# Revit family: IS_CeramixBlue_B9494_BIM_DE
name_source: partatom
category: Plumbing Fixtures
revit_build: Autodesk Revit MEP 2015 (Build: 20140606_1530(x64)
units: mm (PartAtom-declared; Revit-internal decimal feet)

## types (1)
- B9494AA - CERAMIX BLUE kitchen mixer one hole single lever hand, low pressure
    Assembly Code = C1030206
    BIMobject category = Taps & Mixers
    BOSUseNativeGeometries = 1
    Brand url = www.idealstandard.com
    Description = B9494AA CERAMIX BLUE kitchen mixer one hole single lever hand, low pressure
    EAN code = https://4015413318730
    Edition number = 1
    FaucetFunction = mixed
    FaucetOperation = leverhandle
    FaucetType = pillar
    FlushRate = 0 m³
    FlushingRate = 0
    IFC Classification = Valve
    IfcExportAs = Valve
    IfcExportType = KITCHEN TAP
    Installation instructions = http://www.idealspec.co.uk
    Manufacturer name = Ideal Standard
    ManufacturerURL = www.idealstandard.com
    Material = Brass
    Material main = Brass
    Model = B9494AA
    ModelNumber = B9494AA
    Name = CERAMIX BLUE kitchen mixer one hole single lever hand, low pressure
    NettWeight = 2,7 kg
    Nominal height = 193
    Nominal width = 56
    NominalDepth = 0 mm  [stored 0 ft]
    NominalHeight = 196 mm
    NominalLength = 289 mm
    NominalWidth = 56 mm  [stored 0.183727 ft]
    OmniClass Code = 23.45.55.17
    OmniClass Description = Mixing Faucets
    Product Guid = 9f1058dd-51dd-4262-b002-5d060f8fc7ca
    Product SKU = B9494
    Product data url = https://bimobject.com
    Product family = CERAMIX BLUE
    Product group = Kitchen Mixer
    Product name = CERAMIX BLUE kitchen mixer one hole single lever hand, low pressure
    Product url = www.idealstandard.de/produkte
    ProductInformation = www.idealstandard.de/produkte
    QR code = http://bimobject.com
    Shape = Sculptured
    Size = 196x189x56 mm
    Space = Internal
    SpareParts = www.idealstandard.de/ersatzteile
    Technical description = www.idealstandard.de\produkte
    URL = www.idealstandard.de
    Uniclass 2015 Code = Pr_40_20_96_45
    Uniclass 2015 Name = Kitchen sinks
    ValveMechanism = ceramic disc
    ValveOperation = lever
    Version = 1
    VolumeUnits = Litres
    WarrantyDurationParts = 5
    WarrantyDurationUnit = year
    Weight Net (Kg) = 2.7
    WorkingPressure = 1-5 Bar

note: [stored X ft] marks values corroborated as IEEE doubles in the binary element streams (Revit-internal decimal feet)

## geometry (parser evidence)
native form markers: Blend x4, Sweep x1
no freeform markers — native parametric forms only
